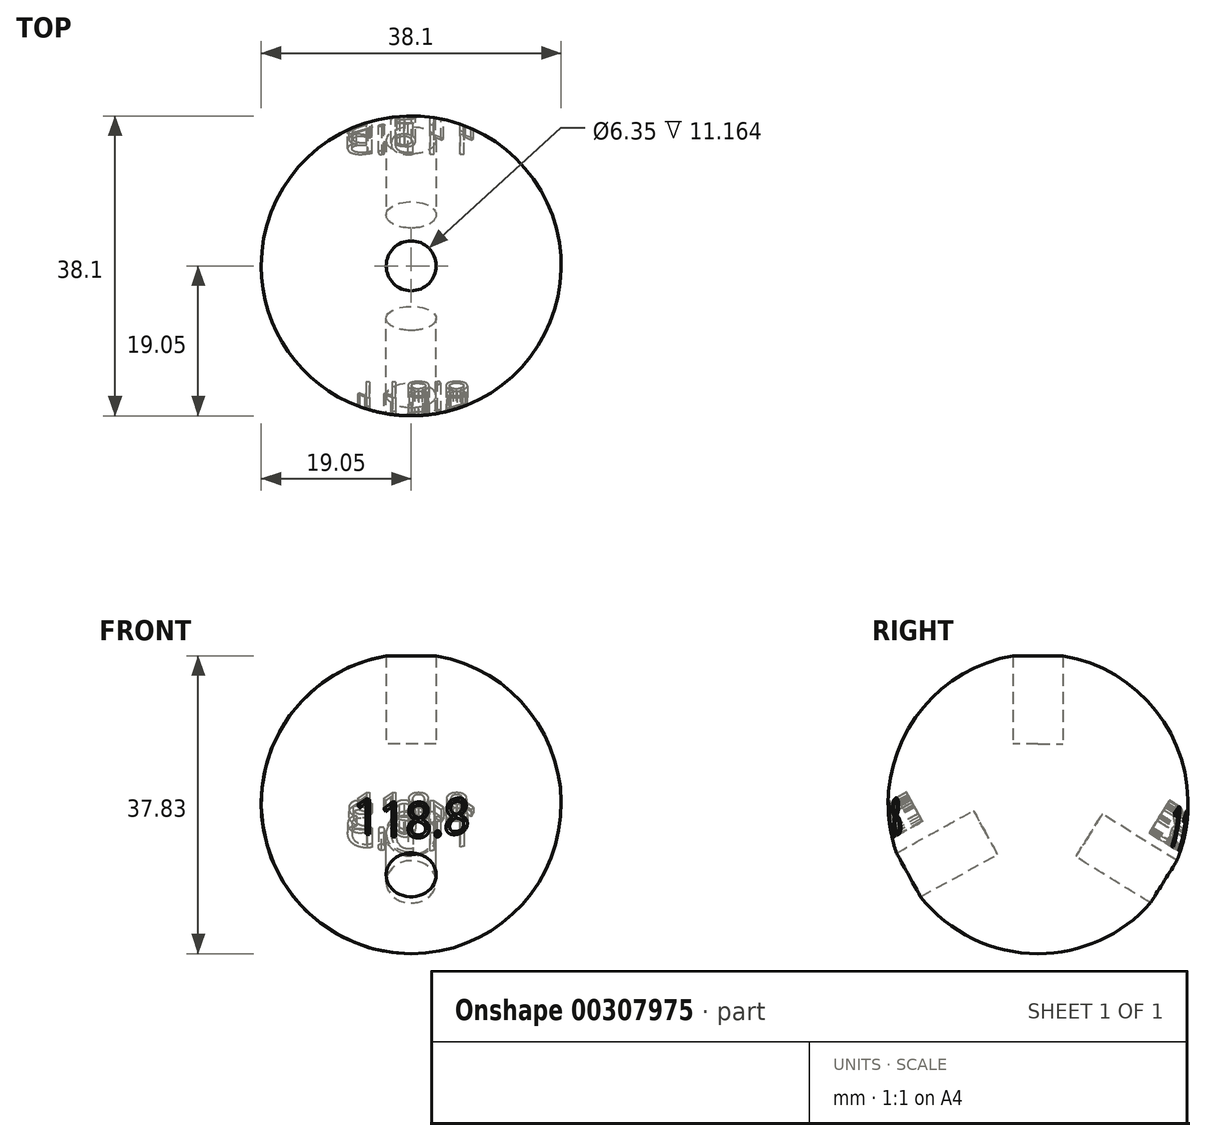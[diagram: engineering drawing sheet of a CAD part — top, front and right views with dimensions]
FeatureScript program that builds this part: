
annotation { "Feature Type Name" : "Feature", "Feature Type Description" : "" }
export const myFeature = defineFeature(function(context is Context, id is Id, definition is map)
    precondition{}
    {
        {
            var Q0;
            Q0=qCreatedBy(makeId("Front.planeOp"),FACE);
            var sketch = newSketch(context, id + "F0", { "sketchPlane" : qUnion([Q0])});
            skArc(sketch, "E0", {"start": v(0, 19.05) * mm, "mid": v(-19.05, 0) * mm, "end": v(0, -19.05) * mm});
            skLineSegment(sketch, "E1", {"start": v(0, 19.05) * mm, "end": v(0, -19.05) * mm});
            skSolve(sketch);
        }
        {
            var Q0;
            Q0=qCreatedBy(makeId("Top.planeOp"),FACE);
            var sketch = newSketch(context, id + "F1", { "sketchPlane" : qUnion([Q0])});
            skCircle(sketch, "E2", {"center": v(0, 0) * mm, "radius": 19.05 * mm});
            skSolve(sketch);
        }
        {
            var Q0;
            Q0=makeQuery(id+"F0.imprint","IMPRINT",FACE,{"disambiguationData":[TD([[makeQuery(id+"F0.imprint","IMPRINT",EDGE,{"derivedFrom":sQuery(id+"F0.wireOp",EDGE,"E0")}),1.0]])]});
            var Q1;
            Q1=sQuery(id+"F1.wireOp",EDGE,"E2");
            revolve(context, id + "F2", {"entities" : qUnion([Q0]), "axis" : qUnion([Q1]), "revolveType" : RevolveType.FULL});
        }
        {
            var Q0;
            Q0=qCreatedBy(makeId("Front.planeOp"),FACE);
            var sketch = newSketch(context, id + "F3", { "sketchPlane" : qUnion([Q0])});
            skLineSegment(sketch, "E3", {"start": v(0, 0) * mm, "end": v(76.32, 0) * mm, "construction": true});
            skLineSegment(sketch, "E4", {"start": v(0, 0) * mm, "end": v(0, 76.7) * mm, "construction": true});
            skSolve(sketch);
        }
        {
            var Q0;
            Q0=qCreatedBy(makeId("Top.planeOp"),FACE);
            cPlane(context, id + "F4", {"entities" : qUnion([Q0]), "cplaneType" : CPlaneType.OFFSET, "offset" : 7.62 * mm, "width" : 152.4 * mm, "height" : 152.4 * mm});
        }
        {
            var Q0;
            Q0=qCreatedBy(id+"F4.planeOp",FACE);
            var sketch = newSketch(context, id + "F5", { "sketchPlane" : qUnion([Q0])});
            skCircle(sketch, "E5", {"center": v(0, 0) * mm, "radius": 3.17 * mm});
            skSolve(sketch);
        }
        {
            var Q0;
            Q0=qSketchRegion(id+"F5",true);
            extrude(context, id + "F6", {"entities" : qUnion([Q0]), "depth" : 76.2 * mm});
        }
        {
            var Q0;
            Q0=makeQuery(id+"F6.opExtrude","SWEPT_BODY",BODY,{"disambiguationData":[OSD([sQuery(id+"F5.wireOp",EDGE,"E5")])]});
            var Q1;
            Q1=sQuery(id+"F3.wireOp",EDGE,"E3");
            transform(context, id + "F7", {"entities" : qUnion([Q0]), "transformType" : TransformType.ROTATION, "transformAxis" : qUnion([Q1]), "angle" : 118.8 * degree, "makeCopy" : true});
        }
        {
            var Q0;
            Q0=makeQuery(id+"F7.opPattern","COPY",BODY,{"derivedFrom":makeQuery(id+"F6.opExtrude","SWEPT_BODY",BODY,{"disambiguationData":[OSD([sQuery(id+"F5.wireOp",EDGE,"E5")])]}),"instanceName":"1"});
            var Q1;
            Q1=sQuery(id+"F3.wireOp",EDGE,"E3");
            transform(context, id + "F8", {"entities" : qUnion([Q0]), "transformType" : TransformType.ROTATION, "transformAxis" : qUnion([Q1]), "angle" : 119.3 * degree, "makeCopy" : true});
        }
        {
            var Q0;
            Q0=makeQuery(id+"F7.opPattern","COPY",FACE,{"derivedFrom":makeQuery(id+"F6.opExtrude","CAP_FACE",FACE,{"disambiguationData":[OSD([sQuery(id+"F5.wireOp",EDGE,"E5")])],"isStart":false}),"instanceName":"1"});
            cPlane(context, id + "F9", {"entities" : qUnion([Q0]), "cplaneType" : CPlaneType.OFFSET, "offset" : 63.5 * mm, "oppositeDirection" : true, "width" : 152.4 * mm, "height" : 152.4 * mm});
        }
        {
            var Q0;
            Q0=qCreatedBy(id+"F9.planeOp",FACE);
            var sketch = newSketch(context, id + "F10", { "sketchPlane" : qUnion([Q0])});
            skText(sketch, "E6", { "text": "118.8 ", "fontName": "OpenSans-Regular.ttf"});
            const initialGuessF10  = {"E6": [-0.00732, 0.00517, 1, 0, 0.00416]};
            skSetInitialGuess(sketch, initialGuessF10);
            skSolve(sketch);
        }
        {
            var Q0;
            Q0=qSketchRegion(id+"F10",true);
            extrude(context, id + "F11", {"entities" : qUnion([Q0]), "operationType" : NewBodyOperationType.REMOVE, "oppositeDirection" : true, "depth" : 6.35 * mm});
        }
        {
            var Q0;
            Q0=makeQuery(id+"F8.opPattern","COPY",FACE,{"derivedFrom":makeQuery(id+"F7.opPattern","COPY",FACE,{"derivedFrom":makeQuery(id+"F6.opExtrude","CAP_FACE",FACE,{"disambiguationData":[OSD([sQuery(id+"F5.wireOp",EDGE,"E5")])],"isStart":false}),"instanceName":"1"}),"instanceName":"1"});
            cPlane(context, id + "F12", {"entities" : qUnion([Q0]), "cplaneType" : CPlaneType.OFFSET, "offset" : 63.5 * mm, "oppositeDirection" : true, "width" : 152.4 * mm, "height" : 152.4 * mm});
        }
        {
            var Q0;
            Q0=qCreatedBy(id+"F12.planeOp",FACE);
            var sketch = newSketch(context, id + "F13", { "sketchPlane" : qUnion([Q0])});
            skText(sketch, "E7", { "text": "119.3", "fontName": "OpenSans-Regular.ttf"});
            const initialGuessF13  = {"E7": [-0.0085, 0.00439, 1, 0, 0.00478]};
            skSetInitialGuess(sketch, initialGuessF13);
            skSolve(sketch);
        }
        {
            var Q0;
            Q0=qSketchRegion(id+"F13",true);
            extrude(context, id + "F14", {"entities" : qUnion([Q0]), "operationType" : NewBodyOperationType.REMOVE, "oppositeDirection" : true, "depth" : 6.35 * mm});
        }
        {
            var Q0;
            Q0=makeQuery(id+"F6.opExtrude","SWEPT_BODY",BODY,{"disambiguationData":[OSD([sQuery(id+"F5.wireOp",EDGE,"E5")])]});
            var Q1;
            Q1=makeQuery(id+"F8.opPattern","COPY",BODY,{"derivedFrom":makeQuery(id+"F7.opPattern","COPY",BODY,{"derivedFrom":makeQuery(id+"F6.opExtrude","SWEPT_BODY",BODY,{"disambiguationData":[OSD([sQuery(id+"F5.wireOp",EDGE,"E5")])]}),"instanceName":"1"}),"instanceName":"1"});
            var Q2;
            Q2=makeQuery(id+"F7.opPattern","COPY",BODY,{"derivedFrom":makeQuery(id+"F6.opExtrude","SWEPT_BODY",BODY,{"disambiguationData":[OSD([sQuery(id+"F5.wireOp",EDGE,"E5")])]}),"instanceName":"1"});
            var Q3;
            Q3=makeQuery(id+"F2.opRevolve","SWEPT_BODY",BODY,{"disambiguationData":[OSD([sQuery(id+"F0.wireOp",EDGE,"E0"),sQuery(id+"F0.wireOp",EDGE,"E1")])]});
            booleanBodies(context, id + "F15", {"operationType" : BooleanOperationType.SUBTRACTION, "tools" : qUnion([Q0, Q1, Q2]), "targets" : qUnion([Q3])});
        }
    });
